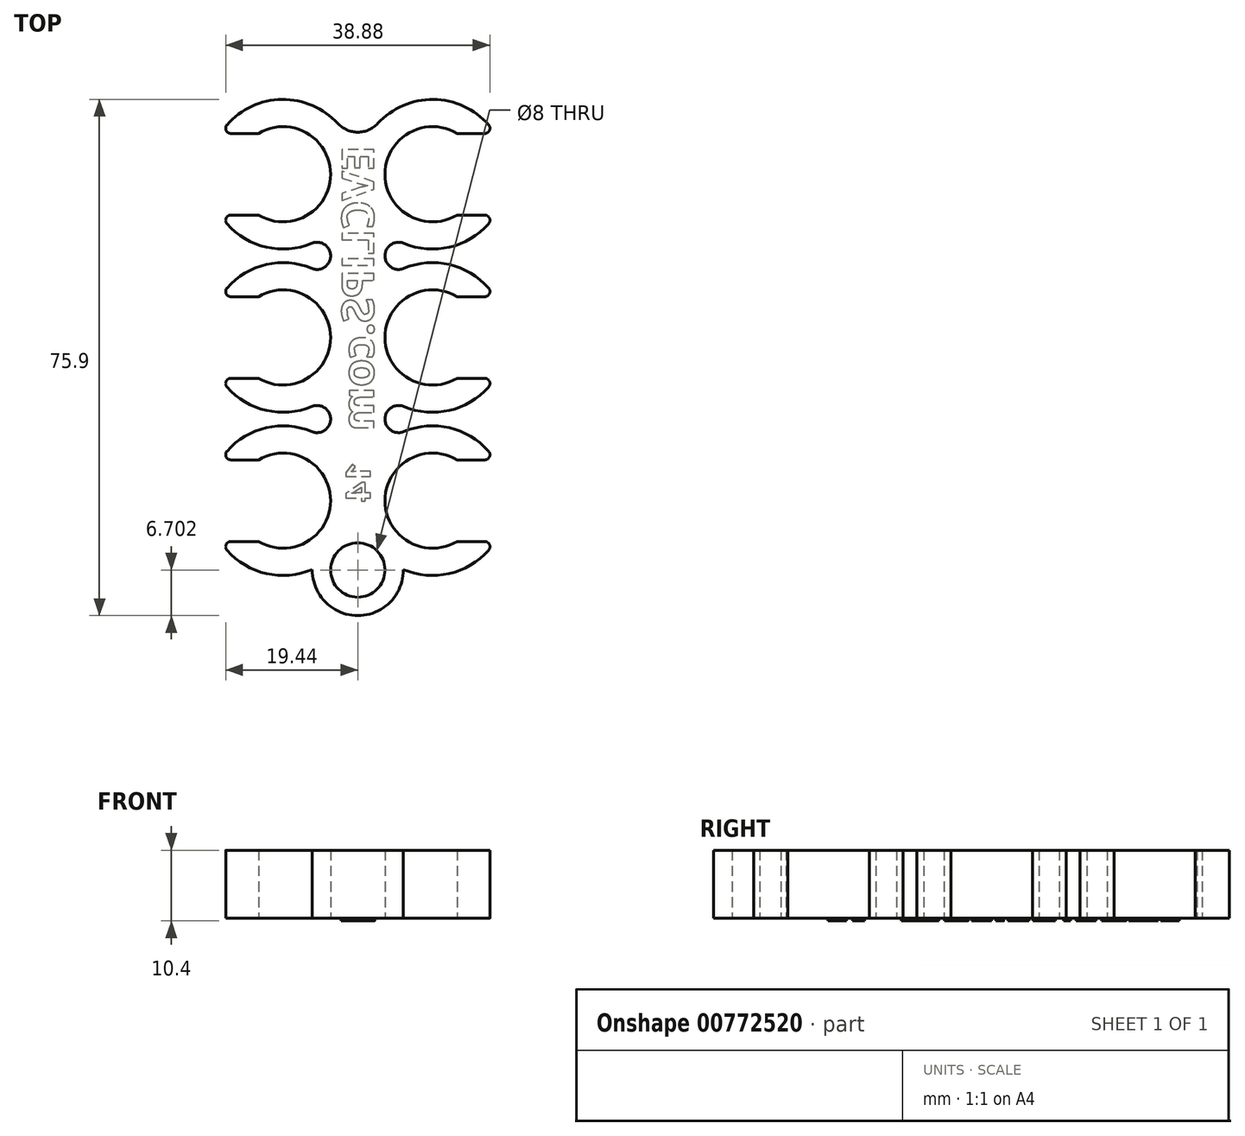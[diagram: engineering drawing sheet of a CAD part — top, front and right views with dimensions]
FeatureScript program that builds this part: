
annotation { "Feature Type Name" : "Feature", "Feature Type Description" : "" }
export const myFeature = defineFeature(function(context is Context, id is Id, definition is map)
    precondition{}
    {
        {
            var Q0;
            Q0=qCreatedBy(makeId("Top.planeOp"),FACE);
            var sketch = newSketch(context, id + "F0", { "sketchPlane" : qUnion([Q0])});
            skLineSegment(sketch, "E0.bottom", {"start": v(-4, 27.5) * mm, "end": v(4, 27.5) * mm});
            skLineSegment(sketch, "E0.top", {"start": v(-4, -27.5) * mm, "end": v(4, -27.5) * mm});
            skLineSegment(sketch, "E0.left", {"start": v(-4, 12) * mm, "end": v(-4, 12) * mm});
            skLineSegment(sketch, "E1.MirrorCS", {"start": v(4, 12) * mm, "end": v(4, 12) * mm});
            skPoint(sketch, "E2.orphan", {"position": v(-2.28, 27.5) * mm});
            skPoint(sketch, "E3.end.orphan", {"position": v(-2.28, -27.5) * mm});
            skPoint(sketch, "E4.MirrorCS.end.orphan", {"position": v(2.28, -27.5) * mm});
            skPoint(sketch, "E4.MirrorCS.start.orphan", {"position": v(2.28, 27.5) * mm});
            skLineSegment(sketch, "E5", {"start": v(-2.28, 27.5) * mm, "end": v(-2.28, -27.5) * mm, "construction": true});
            skLineSegment(sketch, "E6.MirrorCS", {"start": v(2.28, 27.5) * mm, "end": v(2.28, -27.5) * mm, "construction": true});
            skArc(sketch, "E7", {"start": v(-14.6, -6) * mm, "mid": v(-4, 0) * mm, "end": v(-14.6, 6) * mm});
            skArc(sketch, "E8", {"start": v(-19.25, -7.27) * mm, "mid": v(-13.47, -10.72) * mm, "end": v(-6.77, -10.15) * mm});
            skLineSegment(sketch, "E9", {"start": v(-11, 0) * mm, "end": v(-18, 0) * mm, "construction": true});
            skLineSegment(sketch, "E10", {"start": v(-18, 0) * mm, "end": v(-22, 0) * mm, "construction": true});
            skLineSegment(sketch, "E11", {"start": v(0, 0) * mm, "end": v(-29.1, 0) * mm, "construction": true});
            skLineSegment(sketch, "E12.MirrorCS", {"start": v(0, 0) * mm, "end": v(29.1, 0) * mm, "construction": true});
            skLineSegment(sketch, "E13", {"start": v(0, 27.5) * mm, "end": v(0, -27.5) * mm, "construction": true});
            skLineSegment(sketch, "E14", {"start": v(-11, 0) * mm, "end": v(-11, 11) * mm, "construction": true});
            skLineSegment(sketch, "E15", {"start": v(-11, 12) * mm, "end": v(-11, 11) * mm, "construction": true});
            skLineSegment(sketch, "E16", {"start": v(0, 12) * mm, "end": v(-30.87, 12) * mm, "construction": true});
            skLineSegment(sketch, "E17", {"start": v(-11, 0) * mm, "end": v(-11, -11) * mm, "construction": true});
            skLineSegment(sketch, "E18", {"start": v(-11, -12) * mm, "end": v(-11, -11) * mm, "construction": true});
            skLineSegment(sketch, "E19", {"start": v(-30.41, -12) * mm, "end": v(27.29, -12) * mm, "construction": true});
            skLineSegment(sketch, "E20", {"start": v(-11, 7) * mm, "end": v(-28.18, 7) * mm, "construction": true});
            skPoint(sketch, "E20.startSnap0", {"position": v(-11, 5.5) * mm});
            skLineSegment(sketch, "E21", {"start": v(-11, -7) * mm, "end": v(-28.18, -7) * mm, "construction": true});
            skLineSegment(sketch, "E22", {"start": v(-28.18, -7) * mm, "end": v(-28.18, 7) * mm, "construction": true});
            skLineSegment(sketch, "E23", {"start": v(-28.18, 7) * mm, "end": v(-28.18, 6) * mm, "construction": true});
            skLineSegment(sketch, "E24", {"start": v(-28.18, 6) * mm, "end": v(-28.18, 7) * mm, "construction": true});
            skLineSegment(sketch, "E25", {"start": v(-28.18, -7) * mm, "end": v(-28.18, -6) * mm, "construction": true});
            skLineSegment(sketch, "E26", {"start": v(-28.18, -6) * mm, "end": v(-28.18, -7) * mm, "construction": true});
            skLineSegment(sketch, "E27", {"start": v(-18.68, -6) * mm, "end": v(-14.6, -6) * mm});
            skLineSegment(sketch, "E28", {"start": v(-18.68, 6) * mm, "end": v(-14.6, 6) * mm});
            skArc(sketch, "E29.MirrorCS", {"start": v(19.25, -7.27) * mm, "mid": v(13.47, -10.72) * mm, "end": v(6.77, -10.15) * mm});
            skArc(sketch, "E30.MirrorCS", {"start": v(14.6, -6) * mm, "mid": v(4, 0) * mm, "end": v(14.6, 6) * mm});
            skLineSegment(sketch, "E31.MirrorCS", {"start": v(18.68, 6) * mm, "end": v(14.6, 6) * mm});
            skLineSegment(sketch, "E32.MirrorCS", {"start": v(18.68, -6) * mm, "end": v(14.6, -6) * mm});
            skArc(sketch, "E33.MirrorCS", {"start": v(-19.25, 31.27) * mm, "mid": v(-11.14, 35) * mm, "end": v(-2.93, 31.48) * mm});
            skArc(sketch, "E34.MirrorCS", {"start": v(-14.6, 30) * mm, "mid": v(-4, 24) * mm, "end": v(-14.6, 18) * mm});
            skLineSegment(sketch, "E35.MirrorCS", {"start": v(-18.68, 18) * mm, "end": v(-14.6, 18) * mm});
            skLineSegment(sketch, "E36.MirrorCS", {"start": v(-18.68, 30) * mm, "end": v(-14.6, 30) * mm});
            skPoint(sketch, "E37.orphan", {"position": v(-28.18, 30) * mm});
            skPoint(sketch, "E38.orphan", {"position": v(-28.18, 18) * mm});
            skPoint(sketch, "E39.orphan", {"position": v(-11, 18) * mm});
            skPoint(sketch, "E40.orphan", {"position": v(-11, 30) * mm});
            skPoint(sketch, "E41.orphan", {"position": v(11, 6) * mm});
            skPoint(sketch, "E42.orphan", {"position": v(28.18, 6) * mm});
            skPoint(sketch, "E43.orphan", {"position": v(28.18, -6) * mm});
            skPoint(sketch, "E44.orphan", {"position": v(11, -6) * mm});
            skPoint(sketch, "E45.orphan", {"position": v(-11, 6) * mm});
            skPoint(sketch, "E46.orphan", {"position": v(-11, -6) * mm});
            skArc(sketch, "E47.MirrorCS", {"start": v(-14.6, -18) * mm, "mid": v(-4, -24) * mm, "end": v(-14.6, -30) * mm});
            skArc(sketch, "E48.MirrorCS", {"start": v(-19.25, -16.73) * mm, "mid": v(-13.47, -13.28) * mm, "end": v(-6.77, -13.85) * mm});
            skLineSegment(sketch, "E49.MirrorCS", {"start": v(-18.68, -18) * mm, "end": v(-14.6, -18) * mm});
            skLineSegment(sketch, "E50.MirrorCS", {"start": v(-18.68, -30) * mm, "end": v(-14.6, -30) * mm});
            skArc(sketch, "E51.MirrorCS", {"start": v(19.25, -16.73) * mm, "mid": v(13.47, -13.28) * mm, "end": v(6.77, -13.85) * mm});
            skArc(sketch, "E52.MirrorCS", {"start": v(14.6, -18) * mm, "mid": v(4, -24) * mm, "end": v(14.6, -30) * mm});
            skLineSegment(sketch, "E53.MirrorCS", {"start": v(18.68, -18) * mm, "end": v(14.6, -18) * mm});
            skLineSegment(sketch, "E54.MirrorCS", {"start": v(18.68, -30) * mm, "end": v(14.6, -30) * mm});
            skArc(sketch, "E55.MirrorCS", {"start": v(14.6, 30) * mm, "mid": v(4, 24) * mm, "end": v(14.6, 18) * mm});
            skArc(sketch, "E56.MirrorCS", {"start": v(19.25, 31.27) * mm, "mid": v(11.14, 35) * mm, "end": v(2.93, 31.48) * mm});
            skLineSegment(sketch, "E57.MirrorCS", {"start": v(18.68, 18) * mm, "end": v(14.6, 18) * mm});
            skLineSegment(sketch, "E58.MirrorCS", {"start": v(18.68, 30) * mm, "end": v(14.6, 30) * mm});
            skArc(sketch, "E59.trimOffspring", {"start": v(-6.77, 13.85) * mm, "mid": v(-13.47, 13.28) * mm, "end": v(-19.25, 16.73) * mm});
            skArc(sketch, "E60.trimOffspring", {"start": v(6.77, 13.85) * mm, "mid": v(13.47, 13.28) * mm, "end": v(19.25, 16.73) * mm});
            skLineSegment(sketch, "E61.trimOffspring", {"start": v(-4, -12) * mm, "end": v(-4, -12) * mm});
            skArc(sketch, "E62.trimOffspring", {"start": v(-6.77, 10.15) * mm, "mid": v(-13.47, 10.72) * mm, "end": v(-19.25, 7.27) * mm});
            skArc(sketch, "E63.trimOffspring", {"start": v(6.77, 10.15) * mm, "mid": v(13.47, 10.72) * mm, "end": v(19.25, 7.27) * mm});
            skLineSegment(sketch, "E64.trimOffspring", {"start": v(4, -12) * mm, "end": v(4, -12) * mm});
            skArc(sketch, "E65.trimOffspring", {"start": v(2.93, -31.48) * mm, "mid": v(11.14, -35) * mm, "end": v(19.25, -31.27) * mm});
            skArc(sketch, "E66.trimOffspring", {"start": v(-2.93, -31.48) * mm, "mid": v(-11.14, -35) * mm, "end": v(-19.25, -31.27) * mm});
            skPoint(sketch, "E67.visualSharp", {"position": v(0, -24) * mm});
            skArc(sketch, "E67.filletArc", {"start": v(2.93, -31.48) * mm, "mid": v(0, -30.2) * mm, "end": v(-2.93, -31.48) * mm});
            skPoint(sketch, "E68.visualSharp", {"position": v(-4, -15.51) * mm});
            skArc(sketch, "E68.filletArc", {"start": v(-6.77, -13.85) * mm, "mid": v(-4.9, -13.66) * mm, "end": v(-4, -12) * mm});
            skPoint(sketch, "E69.visualSharp", {"position": v(-4, -8.49) * mm});
            skArc(sketch, "E69.filletArc", {"start": v(-4, -12) * mm, "mid": v(-4.9, -10.34) * mm, "end": v(-6.77, -10.15) * mm});
            skPoint(sketch, "E70.visualSharp", {"position": v(4, -15.51) * mm});
            skArc(sketch, "E70.filletArc", {"start": v(4, -12) * mm, "mid": v(4.9, -13.66) * mm, "end": v(6.77, -13.85) * mm});
            skPoint(sketch, "E71.visualSharp", {"position": v(4, -8.49) * mm});
            skArc(sketch, "E71.filletArc", {"start": v(6.77, -10.15) * mm, "mid": v(4.9, -10.34) * mm, "end": v(4, -12) * mm});
            skPoint(sketch, "E72.visualSharp", {"position": v(-4, 8.49) * mm});
            skArc(sketch, "E72.filletArc", {"start": v(-6.77, 10.15) * mm, "mid": v(-4.9, 10.34) * mm, "end": v(-4, 12) * mm});
            skPoint(sketch, "E73.visualSharp", {"position": v(-4, 15.51) * mm});
            skArc(sketch, "E73.filletArc", {"start": v(-4, 12) * mm, "mid": v(-4.9, 13.66) * mm, "end": v(-6.77, 13.85) * mm});
            skPoint(sketch, "E74.visualSharp", {"position": v(4, 8.49) * mm});
            skArc(sketch, "E74.filletArc", {"start": v(4, 12) * mm, "mid": v(4.9, 10.34) * mm, "end": v(6.77, 10.15) * mm});
            skPoint(sketch, "E75.visualSharp", {"position": v(4, 15.51) * mm});
            skArc(sketch, "E75.filletArc", {"start": v(6.77, 13.85) * mm, "mid": v(4.9, 13.66) * mm, "end": v(4, 12) * mm});
            skArc(sketch, "E76.filletArc", {"start": v(-2.93, 31.48) * mm, "mid": v(0, 30.2) * mm, "end": v(2.93, 31.48) * mm});
            skPoint(sketch, "E77.visualSharp", {"position": v(-20.22, -30) * mm});
            skArc(sketch, "E77.filletArc", {"start": v(-18.68, -30) * mm, "mid": v(-19.37, -30.45) * mm, "end": v(-19.25, -31.27) * mm});
            skPoint(sketch, "E78.visualSharp", {"position": v(-20.22, -18) * mm});
            skArc(sketch, "E78.filletArc", {"start": v(-19.25, -16.73) * mm, "mid": v(-19.37, -17.55) * mm, "end": v(-18.68, -18) * mm});
            skPoint(sketch, "E79.visualSharp", {"position": v(20.22, -30) * mm});
            skArc(sketch, "E79.filletArc", {"start": v(19.25, -31.27) * mm, "mid": v(19.37, -30.45) * mm, "end": v(18.68, -30) * mm});
            skPoint(sketch, "E80.visualSharp", {"position": v(20.22, -18) * mm});
            skArc(sketch, "E80.filletArc", {"start": v(18.68, -18) * mm, "mid": v(19.37, -17.55) * mm, "end": v(19.25, -16.73) * mm});
            skPoint(sketch, "E81.visualSharp", {"position": v(20.22, -6) * mm});
            skArc(sketch, "E81.filletArc", {"start": v(19.25, -7.27) * mm, "mid": v(19.37, -6.45) * mm, "end": v(18.68, -6) * mm});
            skPoint(sketch, "E82.visualSharp", {"position": v(20.22, 6) * mm});
            skArc(sketch, "E82.filletArc", {"start": v(18.68, 6) * mm, "mid": v(19.37, 6.45) * mm, "end": v(19.25, 7.27) * mm});
            skPoint(sketch, "E83.visualSharp", {"position": v(-20.22, 6) * mm});
            skArc(sketch, "E83.filletArc", {"start": v(-19.25, 7.27) * mm, "mid": v(-19.37, 6.45) * mm, "end": v(-18.68, 6) * mm});
            skPoint(sketch, "E84.visualSharp", {"position": v(-20.22, -6) * mm});
            skArc(sketch, "E84.filletArc", {"start": v(-18.68, -6) * mm, "mid": v(-19.37, -6.45) * mm, "end": v(-19.25, -7.27) * mm});
            skPoint(sketch, "E85.visualSharp", {"position": v(20.22, 18) * mm});
            skArc(sketch, "E85.filletArc", {"start": v(19.25, 16.73) * mm, "mid": v(19.37, 17.55) * mm, "end": v(18.68, 18) * mm});
            skPoint(sketch, "E86.visualSharp", {"position": v(-20.22, 18) * mm});
            skArc(sketch, "E86.filletArc", {"start": v(-18.68, 18) * mm, "mid": v(-19.37, 17.55) * mm, "end": v(-19.25, 16.73) * mm});
            skPoint(sketch, "E87.visualSharp", {"position": v(20.22, 30) * mm});
            skArc(sketch, "E87.filletArc", {"start": v(18.68, 30) * mm, "mid": v(19.37, 30.45) * mm, "end": v(19.25, 31.27) * mm});
            skPoint(sketch, "E88.visualSharp", {"position": v(-20.22, 30) * mm});
            skArc(sketch, "E88.filletArc", {"start": v(-19.25, 31.27) * mm, "mid": v(-19.37, 30.45) * mm, "end": v(-18.68, 30) * mm});
            skLineSegment(sketch, "E89", {"start": v(0, -27.5) * mm, "end": v(0, -44.4) * mm, "construction": true});
            skCircle(sketch, "E90", {"center": v(0, -34.2) * mm, "radius": 6.7 * mm});
            skCircle(sketch, "E91", {"center": v(0, -34.2) * mm, "radius": 4 * mm});
            skSolve(sketch);
        }
        {
            var Q0;
            Q0=makeQuery(id+"F0.imprint","IMPRINT",FACE,{"disambiguationData":[TD([[makeQuery(id+"F0.imprint","IMPRINT",EDGE,{"derivedFrom":sQuery(id+"F0.wireOp",EDGE,"E7")}),-1.0]])]});
            extrude(context, id + "F1", {"entities" : qUnion([Q0]), "depth" : 10 * mm, "offsetDistance" : 25 * mm});
        }
        {
            var Q0;
            {var subQ0=sQuery(id+"F0.wireOp",EDGE,"E85.filletArc");var subQ1=sQuery(id+"F0.wireOp",EDGE,"E84.filletArc");var subQ2=sQuery(id+"F0.wireOp",EDGE,"E83.filletArc");var subQ3=sQuery(id+"F0.wireOp",EDGE,"E82.filletArc");var subQ4=sQuery(id+"F0.wireOp",EDGE,"E81.filletArc");var subQ5=sQuery(id+"F0.wireOp",EDGE,"E80.filletArc");var subQ6=sQuery(id+"F0.wireOp",EDGE,"E79.filletArc");var subQ7=sQuery(id+"F0.wireOp",EDGE,"E78.filletArc");var subQ8=sQuery(id+"F0.wireOp",EDGE,"E77.filletArc");var subQ9=sQuery(id+"F0.wireOp",EDGE,"E76.filletArc");var subQ10=sQuery(id+"F0.wireOp",EDGE,"E75.filletArc");var subQ11=sQuery(id+"F0.wireOp",EDGE,"E74.filletArc");var subQ12=sQuery(id+"F0.wireOp",EDGE,"E73.filletArc");var subQ13=sQuery(id+"F0.wireOp",EDGE,"E72.filletArc");var subQ14=sQuery(id+"F0.wireOp",EDGE,"E71.filletArc");var subQ15=sQuery(id+"F0.wireOp",EDGE,"E70.filletArc");var subQ16=sQuery(id+"F0.wireOp",EDGE,"E69.filletArc");var subQ17=sQuery(id+"F0.wireOp",EDGE,"E68.filletArc");var subQ18=sQuery(id+"F0.wireOp",EDGE,"E67.filletArc");var subQ19=sQuery(id+"F0.wireOp",EDGE,"E66.trimOffspring");var subQ20=sQuery(id+"F0.wireOp",EDGE,"E65.trimOffspring");var subQ21=sQuery(id+"F0.wireOp",EDGE,"E63.trimOffspring");var subQ22=sQuery(id+"F0.wireOp",EDGE,"E62.trimOffspring");var subQ23=sQuery(id+"F0.wireOp",EDGE,"E60.trimOffspring");var subQ24=sQuery(id+"F0.wireOp",EDGE,"E59.trimOffspring");var subQ25=sQuery(id+"F0.wireOp",EDGE,"E58.MirrorCS");var subQ26=sQuery(id+"F0.wireOp",EDGE,"E57.MirrorCS");var subQ27=sQuery(id+"F0.wireOp",EDGE,"E33.MirrorCS");var subQ28=sQuery(id+"F0.wireOp",EDGE,"E32.MirrorCS");var subQ29=sQuery(id+"F0.wireOp",EDGE,"E31.MirrorCS");var subQ30=sQuery(id+"F0.wireOp",EDGE,"E30.MirrorCS");var subQ31=sQuery(id+"F0.wireOp",EDGE,"E29.MirrorCS");var subQ32=sQuery(id+"F0.wireOp",EDGE,"E34.MirrorCS");var subQ33=sQuery(id+"F0.wireOp",EDGE,"E86.filletArc");var subQ34=sQuery(id+"F0.wireOp",EDGE,"E7");var subQ35=sQuery(id+"F0.wireOp",EDGE,"E56.MirrorCS");var subQ36=sQuery(id+"F0.wireOp",EDGE,"E28");var subQ37=sQuery(id+"F0.wireOp",EDGE,"E8");var subQ38=sQuery(id+"F0.wireOp",EDGE,"E27");var subQ39=sQuery(id+"F0.wireOp",EDGE,"E35.MirrorCS");var subQ40=sQuery(id+"F0.wireOp",EDGE,"E36.MirrorCS");var subQ41=sQuery(id+"F0.wireOp",EDGE,"E47.MirrorCS");var subQ42=sQuery(id+"F0.wireOp",EDGE,"E48.MirrorCS");var subQ43=sQuery(id+"F0.wireOp",EDGE,"E49.MirrorCS");var subQ44=sQuery(id+"F0.wireOp",EDGE,"E50.MirrorCS");var subQ45=sQuery(id+"F0.wireOp",EDGE,"E51.MirrorCS");var subQ46=sQuery(id+"F0.wireOp",EDGE,"E52.MirrorCS");var subQ47=sQuery(id+"F0.wireOp",EDGE,"E53.MirrorCS");var subQ48=sQuery(id+"F0.wireOp",EDGE,"E54.MirrorCS");var subQ49=sQuery(id+"F0.wireOp",EDGE,"E55.MirrorCS");var subQ50=sQuery(id+"F0.wireOp",EDGE,"E87.filletArc");var subQ51=sQuery(id+"F0.wireOp",EDGE,"E88.filletArc");Q0=makeQuery(id+"FhVumSFSnemjP5f_1.boolean.opBoolean","SPLIT",FACE,{"disambiguationData":[TD([makeQuery(id+"F1.opExtrude","SWEPT_FACE",FACE,{"disambiguationData":[OSD([subQ34])]})])],"derivedFrom":makeQuery(id+"F1.opExtrude","CAP_FACE",FACE,{"disambiguationData":[OSD([subQ34,subQ37,subQ38,subQ36,subQ31,subQ30,subQ29,subQ28,subQ27,subQ32,subQ39,subQ40,subQ41,subQ42,subQ43,subQ44,subQ45,subQ46,subQ47,subQ48,subQ49,subQ35,subQ26,subQ25,subQ24,subQ23,subQ22,subQ21,subQ20,subQ19,subQ18,subQ17,subQ16,subQ15,subQ14,subQ13,subQ12,subQ11,subQ10,subQ9,subQ8,subQ7,subQ6,subQ5,subQ4,subQ3,subQ2,subQ1,subQ0,subQ33,subQ50,subQ51])],"isStart":true})});}
            var sketch = newSketch(context, id + "F2", { "sketchPlane" : qUnion([Q0])});
            skLineSegment(sketch, "E92", {"start": v(0, -30.2) * mm, "end": v(0, 15.7) * mm, "construction": true});
            skLineSegment(sketch, "E93.bottom", {"start": v(3, 13.7) * mm, "end": v(-1.78, 13.7) * mm, "construction": true});
            skLineSegment(sketch, "E93.left", {"start": v(3, 13.7) * mm, "end": v(3, -30.2) * mm, "construction": true});
            skPoint(sketch, "E93.middle", {"position": v(1.59, -18.33) * mm});
            skLineSegment(sketch, "E94", {"start": v(3, -30.2) * mm, "end": v(3.23, -30.2) * mm, "construction": true});
            skLineSegment(sketch, "E95", {"start": v(3, -28.2) * mm, "end": v(3, -28.2) * mm});
            skText(sketch, "E96", { "text": "EVCLIPS.com\n", "fontName": "OpenSans-Bold.ttf"});
            skLineSegment(sketch, "E97", {"start": v(0, 20.7) * mm, "end": v(0, 30.2) * mm, "construction": true});
            skLineSegment(sketch, "E98.bottom", {"start": v(3, 27.26) * mm, "end": v(-3, 27.26) * mm, "construction": true});
            skLineSegment(sketch, "E98.top", {"start": v(3, 23.63) * mm, "end": v(-3, 23.63) * mm, "construction": true});
            skLineSegment(sketch, "E98.left", {"start": v(3, 27.26) * mm, "end": v(3, 23.63) * mm, "construction": true});
            skLineSegment(sketch, "E98.right", {"start": v(-3, 27.26) * mm, "end": v(-3, 23.63) * mm, "construction": true});
            skPoint(sketch, "E98.middle", {"position": v(0, 25.45) * mm});
            skText(sketch, "E99", { "text": "14", "fontName": "OpenSans-Bold.ttf"});
            skLineSegment(sketch, "E100", {"start": v(-2.4, -26.93) * mm, "end": v(-2.4, 17.7) * mm, "construction": true});
            skLineSegment(sketch, "E101", {"start": v(-2.4, -5.5) * mm, "end": v(3, -5.5) * mm, "construction": true});
            const initialGuessF2  = {"E96": [0.00238, -0.0282, 0, 1, 0.00478], "E99": [0.00185, 0.01838, 0, 1, 0.00363]};
            skSetInitialGuess(sketch, initialGuessF2);
            skSolve(sketch);
        }
        {
            var Q0;
            Q0=qSketchRegion(id+"F2",true);
            extrude(context, id + "F3", {"entities" : qUnion([Q0]), "operationType" : NewBodyOperationType.ADD, "depth" : 0.4 * mm, "offsetDistance" : 25 * mm});
        }
        {
            var Q0;
            {var subQ0=sQuery(id+"F0.wireOp",EDGE,"E91");var subQ1=sQuery(id+"F0.wireOp",EDGE,"E65.trimOffspring");var subQ2=makeQuery(id+"F0.imprint","INTERSECT",VERTEX,{"derivedFrom":[subQ1,subQ0]});Q0=makeQuery(id+"F0.imprint","IMPRINT",FACE,{"disambiguationData":[TD([[makeQuery(id+"F0.imprint","IMPRINT",EDGE,{"disambiguationData":[TD([[subQ2,-1.0]])],"derivedFrom":subQ1}),-1.0]])]});}
            var Q1;
            {var subQ0=sQuery(id+"F0.wireOp",EDGE,"E90");var subQ1=makeQuery(id+"F0.imprint","IMPRINT",VERTEX,{"derivedFrom":subQ0});Q1=makeQuery(id+"F0.imprint","IMPRINT",FACE,{"disambiguationData":[TD([[makeQuery(id+"F0.imprint","IMPRINT",EDGE,{"disambiguationData":[TD([[subQ1,1.0]])],"derivedFrom":subQ0}),1.0]])]});}
            extrude(context, id + "F4", {"entities" : qUnion([Q0, Q1]), "operationType" : NewBodyOperationType.ADD, "depth" : 10 * mm, "offsetDistance" : 25 * mm});
        }
    });
